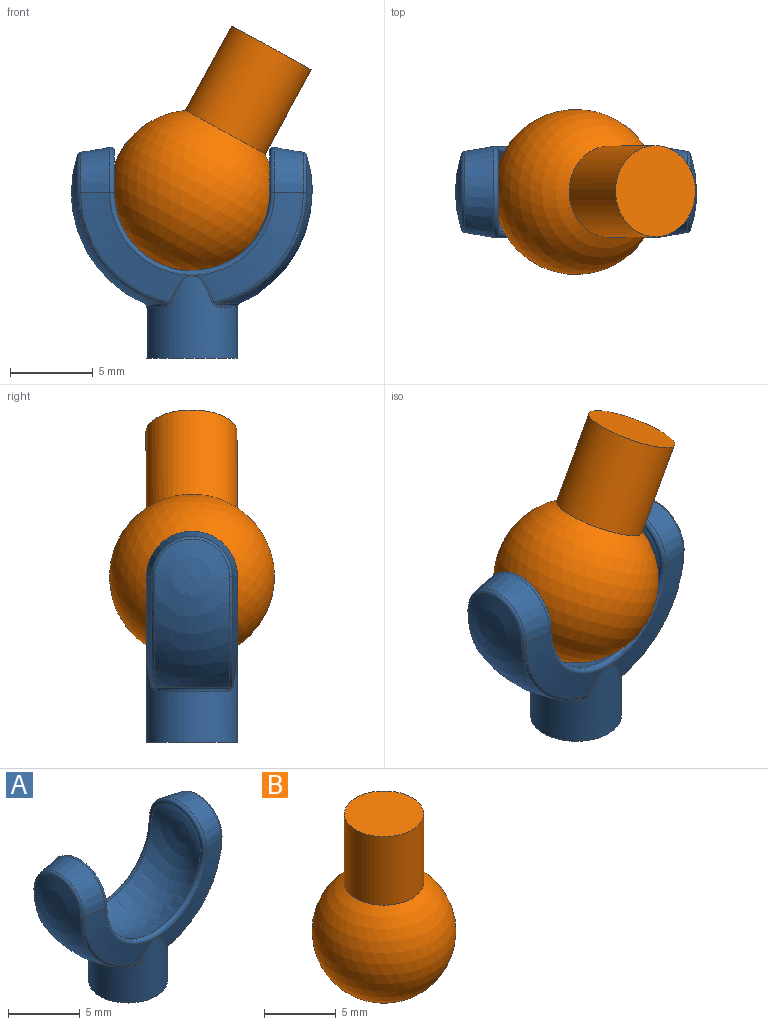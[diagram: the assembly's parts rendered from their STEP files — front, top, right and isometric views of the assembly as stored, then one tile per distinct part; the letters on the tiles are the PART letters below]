
ASSEMBLY  parts=2 mates=1
PART A: 33 faces, bbox 15x14.1x17.1 mm
  f0: sphere r=7.3mm, area 48.5mm2, adj f4,f8,f13,f27
  f1: sphere r=7.3mm, area 48.5mm2, adj f5,f9,f18,f26
  f2: cone r=6.74mm half-angle=80deg, axis (0,-1,0), area 14.7mm2, adj f4,f12,f14,f23
  f3: cone r=6.74mm half-angle=80deg, axis (0,-1,0), area 14.7mm2, adj f5,f14,f17,f22
  f4: torus R=6.7mm, axis (0,1,0), area 2.5mm2, adj f0,f2,f13,f25
  f5: torus R=6.7mm, axis (0,1,0), area 2.5mm2, adj f1,f3,f18,f24
  f6: cone r=6.74mm half-angle=80deg, axis (0,1,0), area 14.7mm2, adj f9,f15,f17,f30
  f7: cone r=6.74mm half-angle=80deg, axis (0,1,0), area 14.7mm2, adj f8,f12,f15,f31
  f8: torus R=6.7mm, axis (0,-1,0), area 2.5mm2, adj f0,f7,f13,f29
  f9: torus R=6.7mm, axis (0,-1,0), area 2.5mm2, adj f1,f6,f18,f28
  f10: sphere r=5.3mm, area 98.9mm2, adj f11,f14,f15,f16
  f11: torus R=2.51mm, axis (-1,0,0), area 4.6mm2, adj f10,f12,f14,f15
  f12: cone r=2.45mm half-angle=10deg, axis (1,0,0), area 14.5mm2, adj f2,f7,f11,f13
  f13: torus R=2.2mm, axis (-1,0,0), area 2mm2, adj f0,f4,f8,f12
  f14: torus R=4.95mm, axis (0,1,0), area 8.3mm2, adj f2,f3,f10,f11,f16,f21
  f15: torus R=4.95mm, axis (0,-1,0), area 8.3mm2, adj f6,f7,f10,f11,f16,f32
  f16: torus R=2.51mm, axis (1,0,0), area 4.6mm2, adj f10,f14,f15,f17
  f17: cone r=2.45mm half-angle=10deg, axis (-1,0,0), area 14.5mm2, adj f3,f6,f16,f18
  f18: torus R=2.2mm, axis (1,0,0), area 2mm2, adj f1,f5,f9,f17
  f19: cylinder r=2.76mm len=5.51mm, axis (0,0,1), area 60.3mm2, adj f20,f21,f22,f23,f24,f25,f26,f27
  f20: plane 5.51x5.51mm, normal (0,0,-1), area 23.9mm2, adj f19
  f21: bspline ~0.47x0.09mm, area 0mm2, adj f14,f19,f22,f23
  f22: bspline ~2.69x1.63mm, area 0.2mm2, adj f3,f19,f21,f24
  f23: bspline ~2.68x1.62mm, area 0.2mm2, adj f2,f19,f21,f25
  f24: bspline ~0.76x0.45mm, area 0.1mm2, adj f5,f19,f22,f26
  f25: bspline ~0.76x0.45mm, area 0.1mm2, adj f4,f19,f23,f27
  f26: torus R=3.01mm, axis (0,0,1), area 1.5mm2, adj f1,f19,f24,f28
  f27: torus R=3.01mm, axis (0,0,1), area 1.5mm2, adj f0,f19,f25,f29
  f28: bspline ~0.76x0.45mm, area 0.1mm2, adj f9,f19,f26,f30
  f29: bspline ~0.76x0.45mm, area 0.1mm2, adj f8,f19,f27,f31
  f30: bspline ~2.68x1.62mm, area 0.2mm2, adj f6,f19,f28,f32
  f31: bspline ~2.69x1.63mm, area 0.2mm2, adj f7,f19,f29,f32
  f32: bspline ~0.47x0.09mm, area 0mm2, adj f15,f19,f30,f31
PART B: 3 faces, bbox 10x10x15 mm
  f0: cylinder r=2.76mm len=5.83mm, axis (0,0,1), area 100.9mm2, adj f1,f2
  f1: sphere r=5mm, area 288.1mm2, adj f0
  f2: plane 5.51x5.51mm, normal (0,0,1), area 23.9mm2, adj f0
PLACE A at identity fixed
PLACE B rot(axis=(0.24,0.29,0.93),82.6deg) t=(0,0,0)mm
MATE ball B.f0 <-> A.f19  axis (0.48,0,0.88) through (0,0,0)mm
